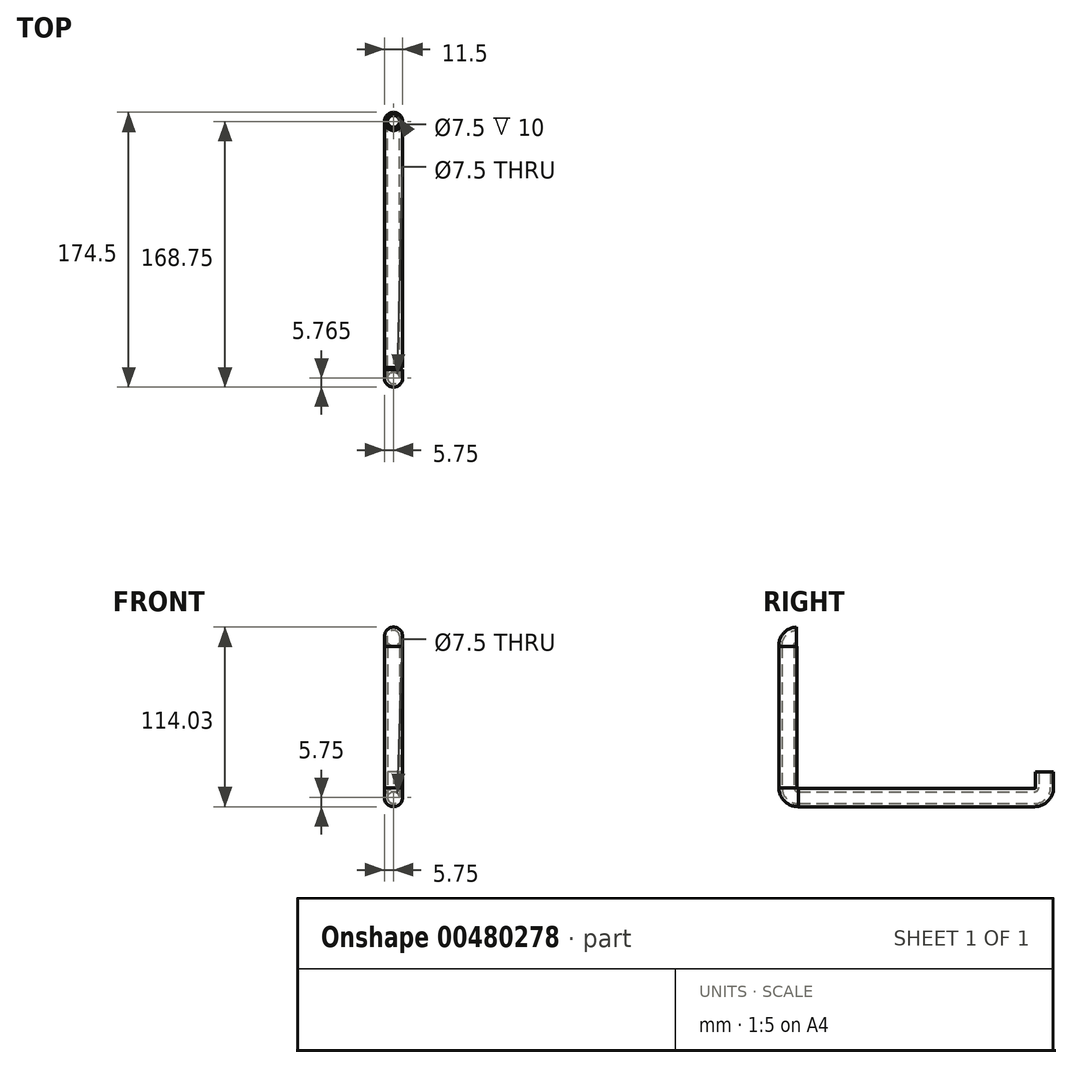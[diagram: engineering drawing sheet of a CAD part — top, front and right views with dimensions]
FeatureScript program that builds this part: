
annotation { "Feature Type Name" : "Feature", "Feature Type Description" : "" }
export const myFeature = defineFeature(function(context is Context, id is Id, definition is map)
    precondition{}
    {
        {
            var Q0;
            Q0=qCreatedBy(makeId("Top.planeOp"),FACE);
            var sketch = newSketch(context, id + "F0", { "sketchPlane" : qUnion([Q0])});
            skCircle(sketch, "E0", {"center": v(0, 0) * mm, "radius": 3.75 * mm});
            skCircle(sketch, "E1", {"center": v(0, 0) * mm, "radius": 5.75 * mm});
            skSolve(sketch);
        }
        {
            var Q0;
            Q0=makeQuery(id+"F0.imprint","IMPRINT",FACE,{"disambiguationData":[TD([[makeQuery(id+"F0.imprint","IMPRINT",EDGE,{"derivedFrom":sQuery(id+"F0.wireOp",EDGE,"E0")}),-1.0]])]});
            extrude(context, id + "F1", {"entities" : qUnion([Q0]), "depth" : 10 * mm, "offsetDistance" : 25 * mm});
        }
        {
            var Q0;
            Q0=qCreatedBy(makeId("Right.planeOp"),FACE);
            var sketch = newSketch(context, id + "F2", { "sketchPlane" : qUnion([Q0])});
            skArc(sketch, "E2", {"start": v(-6.35, -6.35) * mm, "mid": v(-1.86, -4.5) * mm, "end": v(0, 0) * mm});
            skSolve(sketch);
        }
        {
            var Q0;
            Q0=makeQuery(id+"F1.opExtrude","CAP_FACE",FACE,{"disambiguationData":[OSD([sQuery(id+"F0.wireOp",EDGE,"E0"),sQuery(id+"F0.wireOp",EDGE,"E1")])],"isStart":true});
            var Q1;
            Q1=sQuery(id+"F2.wireOp",EDGE,"E2");
            sweep(context, id + "F3", {"operationType" : NewBodyOperationType.ADD, "profiles" : qUnion([Q0]), "path" : qUnion([Q1])});
        }
        {
            var Q0;
            Q0=makeQuery(id+"F3.opSweep","CAP_FACE",FACE,{"disambiguationData":[OSD([sQuery(id+"F0.wireOp",EDGE,"E0"),sQuery(id+"F0.wireOp",EDGE,"E1"),sQuery(id+"F2.wireOp",VERTEX,"E2.start")])],"isStart":false});
            extrude(context, id + "F4", {"entities" : qUnion([Q0]), "operationType" : NewBodyOperationType.ADD, "depth" : 150 * mm, "offsetDistance" : 25 * mm});
        }
        {
            var Q0;
            Q0=qCreatedBy(makeId("Right.planeOp"),FACE);
            var sketch = newSketch(context, id + "F5", { "sketchPlane" : qUnion([Q0])});
            skArc(sketch, "E3", {"start": v(-162.99, 0) * mm, "mid": v(-161.13, -4.5) * mm, "end": v(-156.64, -6.35) * mm});
            skSolve(sketch);
        }
        {
            var Q0;
            Q0=makeQuery(id+"F4.opExtrude","CAP_FACE",FACE,{"disambiguationData":[OSD([sQuery(id+"F0.wireOp",EDGE,"E0"),sQuery(id+"F0.wireOp",EDGE,"E1"),sQuery(id+"F2.wireOp",VERTEX,"E2.start")])],"isStart":false});
            var Q1;
            Q1=sQuery(id+"F5.wireOp",EDGE,"E3");
            sweep(context, id + "F6", {"operationType" : NewBodyOperationType.ADD, "profiles" : qUnion([Q0]), "path" : qUnion([Q1])});
        }
        {
            var Q0;
            Q0=makeQuery(id+"F6.opSweep","CAP_FACE",FACE,{"disambiguationData":[OSD([sQuery(id+"F0.wireOp",EDGE,"E0"),sQuery(id+"F0.wireOp",EDGE,"E1"),sQuery(id+"F2.wireOp",VERTEX,"E2.start"),sQuery(id+"F5.wireOp",VERTEX,"E3.start")])],"isStart":false});
            extrude(context, id + "F7", {"entities" : qUnion([Q0]), "operationType" : NewBodyOperationType.ADD, "depth" : 90 * mm, "offsetDistance" : 25 * mm});
        }
        {
            var Q0;
            Q0=qCreatedBy(makeId("Right.planeOp"),FACE);
            var sketch = newSketch(context, id + "F8", { "sketchPlane" : qUnion([Q0])});
            skArc(sketch, "E4", {"start": v(-157.43, 96.67) * mm, "mid": v(-161.9, 94.53) * mm, "end": v(-163.47, 89.83) * mm});
            skSolve(sketch);
        }
        {
            var Q0;
            Q0=makeQuery(id+"F7.opExtrude","CAP_FACE",FACE,{"disambiguationData":[OSD([sQuery(id+"F0.wireOp",EDGE,"E0"),sQuery(id+"F0.wireOp",EDGE,"E1"),sQuery(id+"F2.wireOp",VERTEX,"E2.start"),sQuery(id+"F5.wireOp",VERTEX,"E3.start")])],"isStart":false});
            var Q1;
            Q1=sQuery(id+"F8.wireOp",EDGE,"E4");
            sweep(context, id + "F9", {"operationType" : NewBodyOperationType.ADD, "profiles" : qUnion([Q0]), "path" : qUnion([Q1])});
        }
    });
